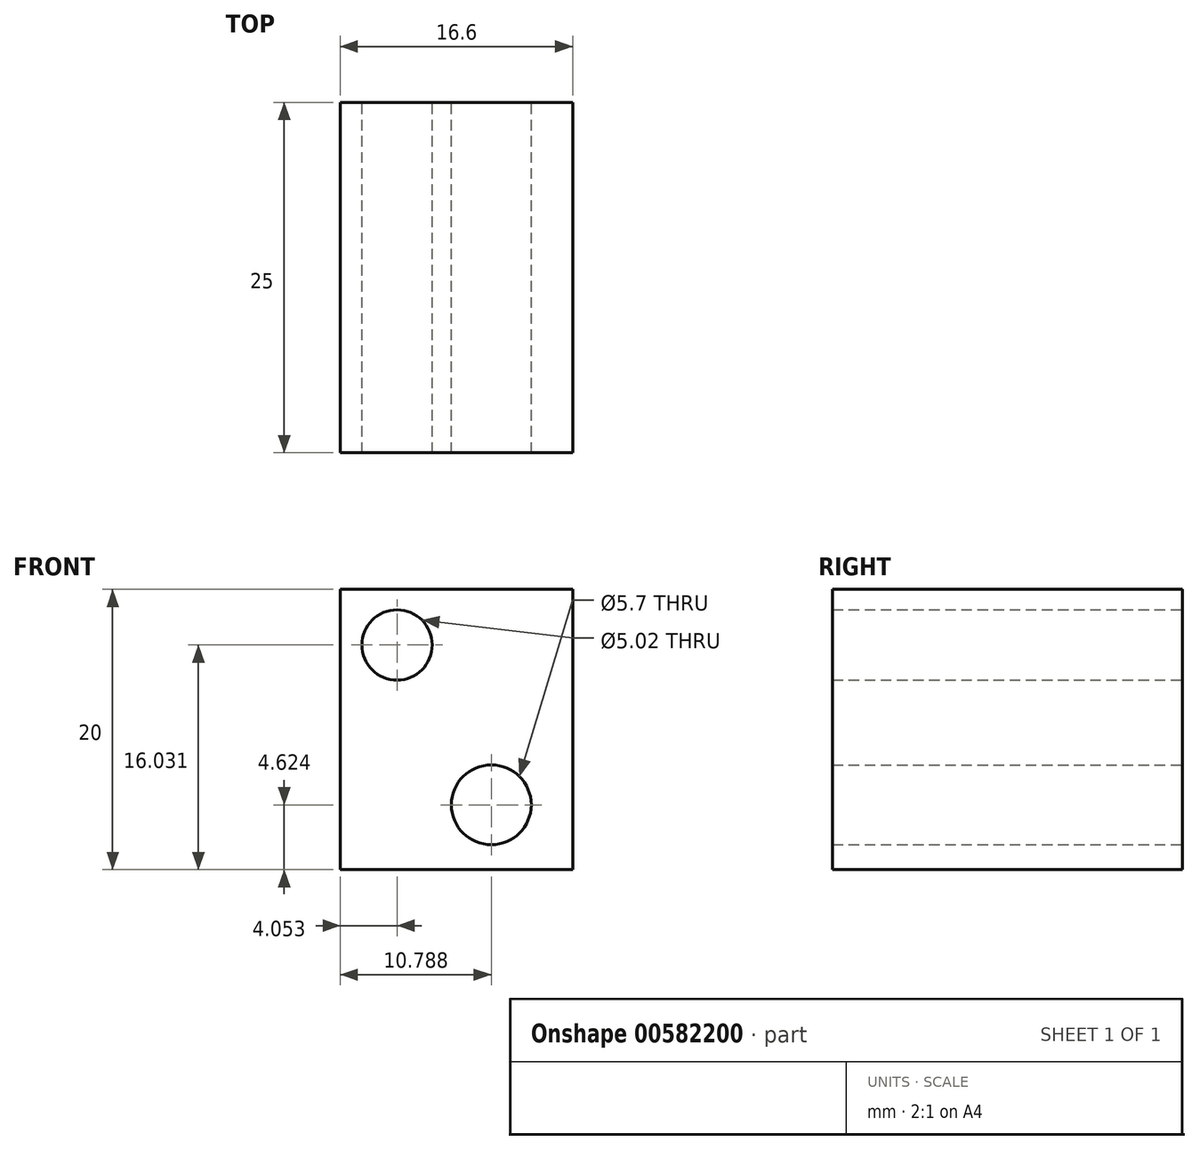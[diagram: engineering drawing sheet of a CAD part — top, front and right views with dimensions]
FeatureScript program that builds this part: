
annotation { "Feature Type Name" : "Feature", "Feature Type Description" : "" }
export const myFeature = defineFeature(function(context is Context, id is Id, definition is map)
    precondition{}
    {
        {
            var Q0;
            Q0=qCreatedBy(makeId("Front.planeOp"),FACE);
            var sketch = newSketch(context, id + "F0", { "sketchPlane" : qUnion([Q0])});
            skLineSegment(sketch, "E0.bottom", {"start": v(-34.87, 38.16) * mm, "end": v(-18.27, 38.16) * mm});
            skLineSegment(sketch, "E0.top", {"start": v(-34.87, 18.16) * mm, "end": v(-18.27, 18.16) * mm});
            skLineSegment(sketch, "E0.left", {"start": v(-34.87, 38.16) * mm, "end": v(-34.87, 18.16) * mm});
            skLineSegment(sketch, "E0.right", {"start": v(-18.27, 38.16) * mm, "end": v(-18.27, 18.16) * mm});
            skSolve(sketch);
        }
        {
            var Q0;
            Q0=makeQuery(id+"F0.imprint","IMPRINT",FACE,{"disambiguationData":[TD([[makeQuery(id+"F0.imprint","IMPRINT",EDGE,{"derivedFrom":sQuery(id+"F0.wireOp",EDGE,"E0.bottom")}),-1.0]])]});
            var sketch = newSketch(context, id + "F1", { "sketchPlane" : qUnion([Q0])});
            skCircle(sketch, "E1", {"center": v(-30.82, 34.2) * mm, "radius": 2.5 * mm});
            skCircle(sketch, "E2", {"center": v(-24.08, 22.78) * mm, "radius": 2.85 * mm});
            skSolve(sketch);
        }
        {
            var Q0;
            Q0=makeQuery(id+"F0.imprint","IMPRINT",FACE,{"disambiguationData":[TD([[makeQuery(id+"F0.imprint","IMPRINT",EDGE,{"derivedFrom":sQuery(id+"F0.wireOp",EDGE,"E0.bottom")}),-1.0]])]});
            extrude(context, id + "F2", {"entities" : qUnion([Q0]), "depth" : 25 * mm, "offsetDistance" : 25 * mm});
        }
        {
            var Q0;
            Q0=makeQuery(id+"F2.opExtrude","CAP_FACE",FACE,{"disambiguationData":[OSD([sQuery(id+"F0.wireOp",EDGE,"E0.bottom"),sQuery(id+"F0.wireOp",EDGE,"E0.top"),sQuery(id+"F0.wireOp",EDGE,"E0.left"),sQuery(id+"F0.wireOp",EDGE,"E0.right")])],"isStart":true});
            var sketch = newSketch(context, id + "F3", { "sketchPlane" : qUnion([Q0])});
            skSolve(sketch);
        }
        {
            var Q0;
            Q0=makeQuery(id+"F1.imprint","IMPRINT",FACE,{"disambiguationData":[TD([[makeQuery(id+"F1.imprint","IMPRINT",EDGE,{"derivedFrom":sQuery(id+"F1.wireOp",EDGE,"E1")}),1.0]])]});
            var Q1;
            Q1=makeQuery(id+"F1.imprint","IMPRINT",FACE,{"disambiguationData":[TD([[makeQuery(id+"F1.imprint","IMPRINT",EDGE,{"derivedFrom":sQuery(id+"F1.wireOp",EDGE,"E2")}),1.0]])]});
            var Q2;
            Q2=sQuery(id+"F1.wireOp",EDGE,"E1");
            var Q3;
            Q3=sQuery(id+"F1.wireOp",EDGE,"E2");
            extrude(context, id + "F4", {"entities" : qUnion([Q0, Q1]), "operationType" : NewBodyOperationType.REMOVE, "surfaceEntities" : qUnion([Q2, Q3]), "depth" : 25 * mm, "offsetDistance" : 25 * mm});
        }
    });
